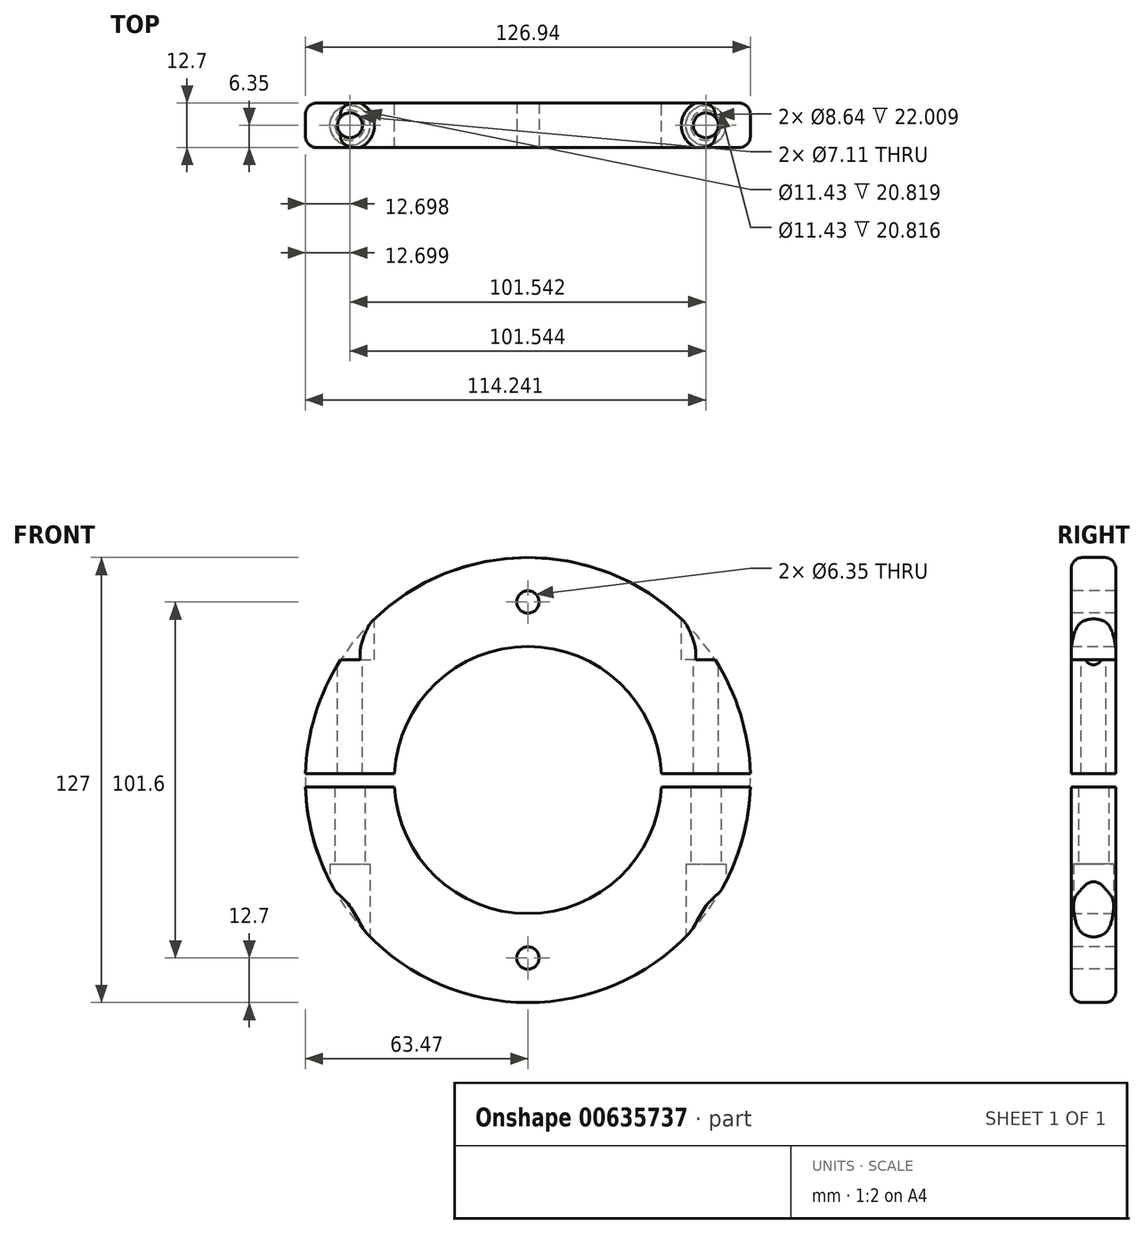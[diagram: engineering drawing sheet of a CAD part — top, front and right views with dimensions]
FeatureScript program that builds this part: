
annotation { "Feature Type Name" : "Feature", "Feature Type Description" : "" }
export const myFeature = defineFeature(function(context is Context, id is Id, definition is map)
    precondition{}
    {
        {
            var Q0;
            Q0=qCreatedBy(makeId("Front.planeOp"),FACE);
            var sketch = newSketch(context, id + "F0", { "sketchPlane" : qUnion([Q0])});
            skArc(sketch, "E0", {"start": v(-38.05, -1.92) * mm, "mid": v(0, -38.1) * mm, "end": v(38.05, -1.92) * mm});
            skArc(sketch, "E1", {"start": v(-63.47, -1.92) * mm, "mid": v(0, -63.5) * mm, "end": v(63.47, -1.92) * mm});
            skLineSegment(sketch, "E2", {"start": v(-63.47, 1.89) * mm, "end": v(-38.05, 1.89) * mm});
            skLineSegment(sketch, "E3", {"start": v(63.47, -1.92) * mm, "end": v(38.05, -1.92) * mm});
            skLineSegment(sketch, "E4.trimOffspring", {"start": v(38.05, 1.89) * mm, "end": v(63.47, 1.89) * mm});
            skLineSegment(sketch, "E5.trimOffspring", {"start": v(-38.05, -1.92) * mm, "end": v(-63.47, -1.92) * mm});
            skPoint(sketch, "E6.orphan", {"position": v(70.78, -1.92) * mm});
            skPoint(sketch, "E7.orphan", {"position": v(70.78, 1.89) * mm});
            skArc(sketch, "E8.trimOffspring", {"start": v(63.47, 1.89) * mm, "mid": v(0, 63.5) * mm, "end": v(-63.47, 1.89) * mm});
            skArc(sketch, "E9.trimOffspring", {"start": v(38.05, 1.89) * mm, "mid": v(0, 38.1) * mm, "end": v(-38.05, 1.89) * mm});
            skSolve(sketch);
        }
        {
            var Q0;
            Q0=makeQuery(id+"F0.imprint","IMPRINT",FACE,{"disambiguationData":[TD([[makeQuery(id+"F0.imprint","IMPRINT",EDGE,{"derivedFrom":sQuery(id+"F0.wireOp",EDGE,"E2")}),1.0]])]});
            var Q1;
            Q1=makeQuery(id+"F0.imprint","IMPRINT",FACE,{"disambiguationData":[TD([[makeQuery(id+"F0.imprint","IMPRINT",EDGE,{"derivedFrom":sQuery(id+"F0.wireOp",EDGE,"E0")}),-1.0]])]});
            extrude(context, id + "F1", {"entities" : qUnion([Q0, Q1]), "endBound" : BoundingType.SYMMETRIC, "depth" : 12.7 * mm, "offsetDistance" : 25.4 * mm});
        }
        {
            var Q0;
            Q0=qCreatedBy(makeId("Top.planeOp"),FACE);
            cPlane(context, id + "F2", {"entities" : qUnion([Q0]), "cplaneType" : CPlaneType.OFFSET, "offset" : 63.5 * mm, "oppositeDirection" : true, "width" : 152.4 * mm, "height" : 152.4 * mm});
        }
        {
            var Q0;
            Q0=qCreatedBy(id+"F2.planeOp",FACE);
            var sketch = newSketch(context, id + "F3", { "sketchPlane" : qUnion([Q0])});
            skPoint(sketch, "E10", {"position": v(50.77, 0) * mm});
            skPoint(sketch, "E11", {"position": v(-50.77, 0) * mm});
            skSolve(sketch);
        }
        {
            var Q0;
            Q0=sQuery(id+"F3.wireOp",VERTEX,"E10");
            var Q1;
            Q1=sQuery(id+"F3.wireOp",VERTEX,"E11");
            var Q2;
            Q2=makeQuery(id+"F1.opExtrude","SWEPT_BODY",BODY,{"disambiguationData":[OSD([sQuery(id+"F0.wireOp",EDGE,"E0"),sQuery(id+"F0.wireOp",EDGE,"E1"),sQuery(id+"F0.wireOp",EDGE,"E3"),sQuery(id+"F0.wireOp",EDGE,"E5.trimOffspring")])]});
            hole(context, id + "F4", {"style" : HoleStyle.C_BORE, "endStyle" : HoleEndStyle.BLIND, "oppositeDirection" : true, "holeDiameter" : 8.64 * mm, "cBoreDiameter" : 11.43 * mm, "cBoreDepth" : 5.08 * mm, "majorDiameter" : 6.35 * mm, "holeDepth" : 38.1 * mm, "isTappedThrough" : true, "tappedDepth" : 12.7 * mm, "tapClearance" : 3, "locations" : qUnion([Q0, Q1]), "scope" : qUnion([Q2])});
        }
        {
            var Q0;
            Q0=qCreatedBy(makeId("Top.planeOp"),FACE);
            cPlane(context, id + "F5", {"entities" : qUnion([Q0]), "cplaneType" : CPlaneType.OFFSET, "offset" : 63.5 * mm, "width" : 152.4 * mm, "height" : 152.4 * mm});
        }
        {
            var Q0;
            Q0=qCreatedBy(id+"F5.planeOp",FACE);
            var sketch = newSketch(context, id + "F6", { "sketchPlane" : qUnion([Q0])});
            skPoint(sketch, "E12", {"position": v(50.77, 0) * mm});
            skPoint(sketch, "E13", {"position": v(-50.77, 0) * mm});
            skSolve(sketch);
        }
        {
            var Q0;
            Q0=sQuery(id+"F6.wireOp",VERTEX,"E12");
            var Q1;
            Q1=sQuery(id+"F6.wireOp",VERTEX,"E13");
            var Q2;
            Q2=makeQuery(id+"F1.opExtrude","SWEPT_BODY",BODY,{"disambiguationData":[OSD([sQuery(id+"F0.wireOp",EDGE,"E2"),sQuery(id+"F0.wireOp",EDGE,"E4.trimOffspring"),sQuery(id+"F0.wireOp",EDGE,"E8.trimOffspring"),sQuery(id+"F0.wireOp",EDGE,"E9.trimOffspring")])]});
            hole(context, id + "F7", {"style" : HoleStyle.C_BORE, "endStyle" : HoleEndStyle.BLIND, "holeDiameter" : 7.11 * mm, "cBoreDiameter" : 13.97 * mm, "cBoreDepth" : 29.2 * mm, "majorDiameter" : 6.35 * mm, "holeDepth" : 63.5 * mm, "isTappedThrough" : true, "tappedDepth" : 12.7 * mm, "tapClearance" : 3, "locations" : qUnion([Q0, Q1]), "scope" : qUnion([Q2])});
        }
        {
            var Q0;
            Q0=makeQuery(id+"F1.opExtrude","CAP_EDGE",EDGE,{"disambiguationData":[OSD([sQuery(id+"F0.wireOp",EDGE,"E8.trimOffspring")])],"isStart":false});
            var Q1;
            Q1=makeQuery(id+"F1.opExtrude","CAP_EDGE",EDGE,{"disambiguationData":[OSD([sQuery(id+"F0.wireOp",EDGE,"E1")])],"isStart":false});
            var Q2;
            Q2=makeQuery(id+"F1.opExtrude","CAP_EDGE",EDGE,{"disambiguationData":[OSD([sQuery(id+"F0.wireOp",EDGE,"E8.trimOffspring")])],"isStart":true});
            var Q3;
            Q3=makeQuery(id+"F1.opExtrude","CAP_EDGE",EDGE,{"disambiguationData":[OSD([sQuery(id+"F0.wireOp",EDGE,"E1")])],"isStart":true});
            fillet(context, id + "F8", {"entities" : qUnion([Q0, Q1, Q2, Q3]), "radius" : 3.17 * mm, "tangentPropagation" : true, "allowEdgeOverflow" : false});
        }
        {
            var Q0;
            Q0=qCreatedBy(makeId("Front.planeOp"),FACE);
            cPlane(context, id + "F9", {"entities" : qUnion([Q0]), "cplaneType" : CPlaneType.OFFSET, "offset" : 25.4 * mm, "width" : 152.4 * mm, "height" : 152.4 * mm});
        }
        {
            var Q0;
            Q0=qCreatedBy(id+"F9.planeOp",FACE);
            var sketch = newSketch(context, id + "F10", { "sketchPlane" : qUnion([Q0])});
            skPoint(sketch, "E14", {"position": v(0, 50.8) * mm});
            skPoint(sketch, "E15", {"position": v(0, -50.8) * mm});
            skSolve(sketch);
        }
        {
            var Q0;
            Q0=sQuery(id+"F10.wireOp",VERTEX,"E14");
            var Q1;
            Q1=sQuery(id+"F10.wireOp",VERTEX,"E15");
            var Q2;
            Q2=makeQuery(id+"F1.opExtrude","SWEPT_BODY",BODY,{"disambiguationData":[OSD([sQuery(id+"F0.wireOp",EDGE,"E0"),sQuery(id+"F0.wireOp",EDGE,"E1"),sQuery(id+"F0.wireOp",EDGE,"E3"),sQuery(id+"F0.wireOp",EDGE,"E5.trimOffspring")])]});
            var Q3;
            Q3=makeQuery(id+"F1.opExtrude","SWEPT_BODY",BODY,{"disambiguationData":[OSD([sQuery(id+"F0.wireOp",EDGE,"E2"),sQuery(id+"F0.wireOp",EDGE,"E4.trimOffspring"),sQuery(id+"F0.wireOp",EDGE,"E8.trimOffspring"),sQuery(id+"F0.wireOp",EDGE,"E9.trimOffspring")])]});
            hole(context, id + "F11", {"style" : HoleStyle.SIMPLE, "endStyle" : HoleEndStyle.BLIND, "holeDiameter" : 6.35 * mm, "majorDiameter" : 6.35 * mm, "holeDepth" : 38.1 * mm, "isTappedThrough" : true, "tappedDepth" : 12.7 * mm, "tapClearance" : 3, "locations" : qUnion([Q0, Q1]), "scope" : qUnion([Q2, Q3])});
        }
    });
